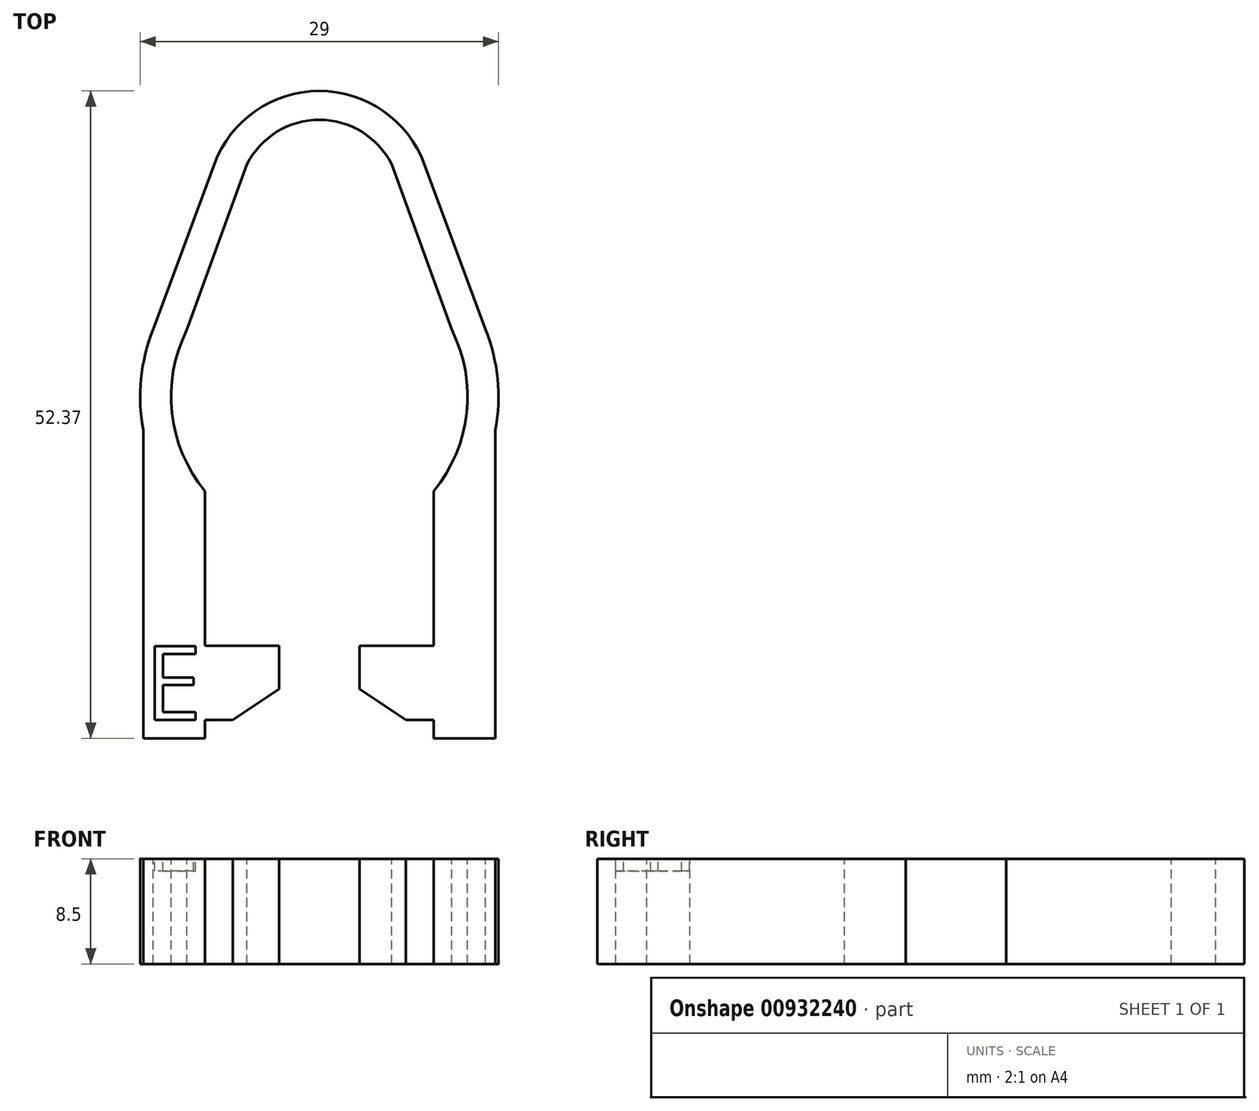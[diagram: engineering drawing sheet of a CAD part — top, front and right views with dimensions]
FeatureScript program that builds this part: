
annotation { "Feature Type Name" : "Feature", "Feature Type Description" : "" }
export const myFeature = defineFeature(function(context is Context, id is Id, definition is map)
    precondition{}
    {
        {
            var Q0;
            Q0=qCreatedBy(makeId("Top.planeOp"),FACE);
            var sketch = newSketch(context, id + "F0", { "sketchPlane" : qUnion([Q0])});
            skPoint(sketch, "E0", {"position": v(0, 0) * mm});
            skPoint(sketch, "E1", {"position": v(-12, 0) * mm});
            skPoint(sketch, "E2", {"position": v(12, 0) * mm});
            skArc(sketch, "E3", {"start": v(-11.67, 2.79) * mm, "mid": v(-11.69, -2.71) * mm, "end": v(-9.25, -7.64) * mm});
            skPoint(sketch, "E4", {"position": v(-10.7, 5.42) * mm});
            skPoint(sketch, "E5", {"position": v(10.7, 5.42) * mm});
            skLineSegment(sketch, "E6", {"start": v(-11.67, 2.79) * mm, "end": v(-11.35, 2.71) * mm, "construction": true});
            skLineSegment(sketch, "E7", {"start": v(11.35, 2.71) * mm, "end": v(11.67, 2.79) * mm, "construction": true});
            skPoint(sketch, "E8", {"position": v(0, -12) * mm});
            skPoint(sketch, "E9", {"position": v(-14.5, 0) * mm});
            skPoint(sketch, "E10", {"position": v(14.5, 0) * mm});
            skArc(sketch, "E11", {"start": v(-14.1, 3.37) * mm, "mid": v(-14.4, 1.7) * mm, "end": v(-14.5, 0) * mm});
            skLineSegment(sketch, "E12", {"start": v(-14.1, 3.37) * mm, "end": v(-13.72, 3.28) * mm, "construction": true});
            skLineSegment(sketch, "E13", {"start": v(13.72, 3.28) * mm, "end": v(14.1, 3.37) * mm, "construction": true});
            skLineSegment(sketch, "E14", {"start": v(-14.5, 0) * mm, "end": v(0, 0) * mm, "construction": true});
            skPoint(sketch, "E15", {"position": v(-9.25, -11.17) * mm});
            skPoint(sketch, "E16", {"position": v(9.25, -11.17) * mm});
            skLineSegment(sketch, "E17", {"start": v(-9.25, -11.17) * mm, "end": v(9.25, -11.17) * mm, "construction": true});
            skLineSegment(sketch, "E18", {"start": v(-9.25, -11.17) * mm, "end": v(-9.25, -20.14) * mm});
            skLineSegment(sketch, "E19", {"start": v(9.25, -11.17) * mm, "end": v(9.25, -20.14) * mm});
            skPoint(sketch, "E20", {"position": v(-14.25, -2.68) * mm});
            skPoint(sketch, "E21", {"position": v(14.25, -2.68) * mm});
            skLineSegment(sketch, "E22", {"start": v(-14.25, -2.68) * mm, "end": v(14.25, -2.68) * mm, "construction": true});
            skLineSegment(sketch, "E23", {"start": v(-14.25, -2.68) * mm, "end": v(-14.25, -21.14) * mm});
            skLineSegment(sketch, "E24", {"start": v(14.25, -2.68) * mm, "end": v(14.25, -21.43) * mm});
            skLineSegment(sketch, "E25", {"start": v(-3.25, -21.14) * mm, "end": v(-3.25, -23.64) * mm});
            skLineSegment(sketch, "E26", {"start": v(-3.25, -23.64) * mm, "end": v(-7, -26.14) * mm});
            skLineSegment(sketch, "E27", {"start": v(-9.25, -27.64) * mm, "end": v(-14.25, -27.64) * mm});
            skLineSegment(sketch, "E28", {"start": v(-14.25, -27.64) * mm, "end": v(-14.25, -21.14) * mm});
            skLineSegment(sketch, "E29", {"start": v(3.25, -21.14) * mm, "end": v(3.25, -23.64) * mm});
            skLineSegment(sketch, "E30", {"start": v(3.25, -23.64) * mm, "end": v(7, -26.14) * mm});
            skLineSegment(sketch, "E31", {"start": v(9.25, -27.64) * mm, "end": v(14.25, -27.64) * mm});
            skLineSegment(sketch, "E32", {"start": v(14.25, -27.64) * mm, "end": v(14.25, -21.43) * mm});
            skLineSegment(sketch, "E33", {"start": v(-14.25, -11.17) * mm, "end": v(-9.25, -11.17) * mm, "construction": true});
            skLineSegment(sketch, "E34", {"start": v(9.25, -11.17) * mm, "end": v(14.25, -11.17) * mm, "construction": true});
            skLineSegment(sketch, "E35", {"start": v(-9.25, -11.17) * mm, "end": v(-9.25, -7.64) * mm});
            skLineSegment(sketch, "E36", {"start": v(9.25, -11.17) * mm, "end": v(9.25, -7.64) * mm});
            skArc(sketch, "E37.trimOffspring", {"start": v(9.25, -7.64) * mm, "mid": v(11.69, -2.71) * mm, "end": v(11.67, 2.79) * mm});
            skArc(sketch, "E38.trimOffspring", {"start": v(14.5, 0) * mm, "mid": v(14.4, 1.7) * mm, "end": v(14.1, 3.37) * mm});
            skArc(sketch, "E39", {"start": v(14.25, -2.68) * mm, "mid": v(14.44, -1.35) * mm, "end": v(14.5, 0) * mm});
            skArc(sketch, "E40.trimOffspring", {"start": v(-14.1, 3.37) * mm, "mid": v(-14.5, 0.35) * mm, "end": v(-14.25, -2.68) * mm});
            skArc(sketch, "E41", {"start": v(9.25, -7.64) * mm, "mid": v(11.93, -1.33) * mm, "end": v(10.7, 5.42) * mm});
            skLineSegment(sketch, "E42", {"start": v(-10.7, 5.42) * mm, "end": v(-5.85, 18.8) * mm});
            skLineSegment(sketch, "E43", {"start": v(10.7, 5.42) * mm, "end": v(5.85, 18.8) * mm});
            skArc(sketch, "E44.trimOffspring", {"start": v(-10.7, 5.42) * mm, "mid": v(-11.93, -1.33) * mm, "end": v(-9.25, -7.64) * mm});
            skLineSegment(sketch, "E45", {"start": v(-9.25, -20.14) * mm, "end": v(-3.25, -20.14) * mm});
            skLineSegment(sketch, "E46", {"start": v(-3.25, -21.14) * mm, "end": v(-3.25, -20.14) * mm});
            skLineSegment(sketch, "E47", {"start": v(9.25, -20.14) * mm, "end": v(3.25, -20.14) * mm});
            skLineSegment(sketch, "E48", {"start": v(3.25, -20.14) * mm, "end": v(3.25, -21.14) * mm});
            skPoint(sketch, "E49.orphan", {"position": v(-9.25, -21.14) * mm});
            skPoint(sketch, "E50.orphan", {"position": v(9.25, -21.43) * mm});
            skLineSegment(sketch, "E51", {"start": v(9.25, -27.64) * mm, "end": v(9.25, -26.14) * mm});
            skLineSegment(sketch, "E52", {"start": v(9.25, -26.14) * mm, "end": v(7, -26.14) * mm});
            skLineSegment(sketch, "E53", {"start": v(-9.25, -27.64) * mm, "end": v(-9.25, -26.14) * mm});
            skLineSegment(sketch, "E54", {"start": v(-9.25, -26.14) * mm, "end": v(-7, -26.14) * mm});
            skArc(sketch, "E55", {"start": v(5.85, 18.8) * mm, "mid": v(0, 22.4) * mm, "end": v(-5.85, 18.8) * mm});
            skPoint(sketch, "E56", {"position": v(0, 22.4) * mm});
            skLineSegment(sketch, "E57", {"start": v(-8.5, 18.8) * mm, "end": v(-5.85, 18.8) * mm, "construction": true});
            skLineSegment(sketch, "E58", {"start": v(5.85, 18.8) * mm, "end": v(8.5, 18.8) * mm, "construction": true});
            skLineSegment(sketch, "E59", {"start": v(-13.36, 5.42) * mm, "end": v(-10.7, 5.42) * mm, "construction": true});
            skLineSegment(sketch, "E60", {"start": v(13.36, 5.42) * mm, "end": v(10.7, 5.42) * mm, "construction": true});
            skArc(sketch, "E61", {"start": v(-13.44, 5.45) * mm, "mid": v(-14.43, 1.44) * mm, "end": v(-14.25, -2.68) * mm});
            skCircle(sketch, "E62", {"center": v(0, 0) * mm, "radius": 12 * mm, "construction": true});
            skArc(sketch, "E63.trimOffspring", {"start": v(14.25, -2.68) * mm, "mid": v(14.43, 1.44) * mm, "end": v(13.44, 5.45) * mm});
            skLineSegment(sketch, "E64", {"start": v(-13.44, 5.45) * mm, "end": v(-8.5, 18.8) * mm});
            skLineSegment(sketch, "E65", {"start": v(13.44, 5.45) * mm, "end": v(8.5, 18.8) * mm});
            skArc(sketch, "E66", {"start": v(8.5, 18.8) * mm, "mid": v(0, 24.73) * mm, "end": v(-8.5, 18.8) * mm});
            skLineSegment(sketch, "E67", {"start": v(0, 24.73) * mm, "end": v(0, -12) * mm, "construction": true});
            skLineSegment(sketch, "E68", {"start": v(-8.5, 18.8) * mm, "end": v(8.5, 18.8) * mm, "construction": true});
            skPoint(sketch, "E69", {"position": v(0, 18.8) * mm});
            skText(sketch, "E70", { "text": "E", "fontName": "OpenSans-Regular.ttf"});
            const initialGuessF0  = {"E70": [-0.01415, -0.02614, 1, 0, 0.006]};
            skSetInitialGuess(sketch, initialGuessF0);
            skSolve(sketch);
        }
        {
            var Q0;
            Q0=makeQuery(id+"F0.imprint","IMPRINT",FACE,{"disambiguationData":[TD([[makeQuery(id+"F0.imprint","IMPRINT",EDGE,{"derivedFrom":sQuery(id+"F0.wireOp",EDGE,"E18")}),-1.0]])]});
            var Q1;
            Q1=makeQuery(id+"F0.imprint","IMPRINT",FACE,{"disambiguationData":[TD([[makeQuery(id+"F0.imprint","IMPRINT",EDGE,{"derivedFrom":sQuery(id+"F0.wireOp",EDGE,"E70.sketch_text.stroke-0")}),-1.0]])]});
            extrude(context, id + "F1", {"entities" : qUnion([Q0, Q1]), "oppositeDirection" : true, "depth" : 8.5 * mm, "offsetDistance" : 25 * mm});
        }
        {
            var Q0;
            Q0=makeQuery(id+"F0.imprint","IMPRINT",FACE,{"disambiguationData":[TD([[makeQuery(id+"F0.imprint","IMPRINT",EDGE,{"derivedFrom":sQuery(id+"F0.wireOp",EDGE,"E70.sketch_text.stroke-0")}),-1.0]])]});
            extrude(context, id + "F2", {"entities" : qUnion([Q0]), "operationType" : NewBodyOperationType.REMOVE, "oppositeDirection" : true, "depth" : 1 * mm, "offsetDistance" : 25 * mm});
        }
    });
